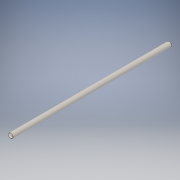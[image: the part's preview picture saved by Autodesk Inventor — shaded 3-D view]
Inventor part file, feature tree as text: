
AUTODESK INVENTOR PART (.ipt)
format: ipt  version: 2019.1 (Build 231200000, 200)  size: 108,544 bytes
history: native  units: in
note: dims shown in document units (in); Inventor stores cm internally (conversion verified against a paired STEP export)
features: fillet x1
ambient origin geometry x8: Origin, YZ Plane, XZ Plane, XY Plane, X Axis, Y Axis, Z Axis, Center Point
bodies: Solid1 (feature_tree)
feature tree (1):
  fillet  "Fillet1"  [1 undecoded]
note: 1 required parameter value undecoded (feature->parameter linkage not recoverable at this tier; creation-order binding heuristic only, values carry confidence <= 0.55)
